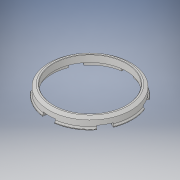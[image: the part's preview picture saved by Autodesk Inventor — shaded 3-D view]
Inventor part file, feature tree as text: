
AUTODESK INVENTOR PART (.ipt)
format: ipt  version: 2018 (Build 220112000, 112)  size: 431,616 bytes
history: native  units: mm
features: reference x28, sketch x14, projected_geometry x11, other x7, extrude x6, sweep x5, fillet x5, chamfer x3, pattern_circular x1
ambient origin geometry x8: Origin, YZ Plane, XZ Plane, XY Plane, X Axis, Y Axis, Z Axis, Center Point
bodies: Volumenkörper1 (feature_tree)
feature tree (80):
  extrude  "Extrusion1"  Depth=2.0mm TaperAngle=45.0deg
  chamfer  "Fase1"  Distance=2.0mm
  extrude  "Extrusion4"  TaperAngle=0.0deg  [1 undecoded]
  sweep  "Sweeping4"
  sketch  "Skizze16"  dims[d29=23.0mm]
  sketch  "Skizze17"  dims[d30=2.0mm d31=0.0mm d32=1.25mm d33=0.174533mm d34=0.174533mm d36=62.65732mm d37=0.174533mm d38=0.174533mm d39=2.0mm d40=0.0mm d43=2.0mm d44=0.0mm d45=0.5mm d46=0.4mm d47=0.5mm d48=0.5mm d49=60.0mm d50=360.0deg d52=0.5mm d53=0.5mm d54=0.0mm d55=0.0mm d56=0.2mm d57=0.0mm d58=0.0mm d59=1.0mm d60=0.25mm d61=2.0mm d62=0.0mm d63=1.25mm d64=1.75mm d65=45.0deg d66=1.0mm]
  sweep  "Sweeping5"
  fillet  "Rundung4"  Radius=0.5mm
  fillet  "Rundung5"  Radius=0.1mm
  extrude  "Extrusion6"  Depth=2.0mm TaperAngle=45.0deg
  pattern_circular  "Runde Anordnung1"  [2 undecoded]
  extrude  "Extrusion7"  Depth=1.25mm
  chamfer  "Fase3"  Distance=0.174533mm
  extrude  "Extrusion2"  Depth=1.25mm
  sketch  "Skizze3"  dims[d5=0.2mm]
  sketch  "Skizze4"  dims[d6=0.2mm]
  sketch  "Skizze6"  dims[d7=0.2mm d8=2.0mm d9=0.0mm]
  sweep  "Sweeping1"
  sweep  "Sweeping2"
  sweep  "Sweeping3"
  chamfer  "Fase2"  Distance=2.0mm
  fillet  "Rundung1"  Radius=0.5mm
  fillet  "Rundung2"  Radius=0.4mm
  extrude  "Extrusion3"  Depth=1.25mm
  fillet  "Rundung3"  Radius=0.5mm
  sketch  "Skizze10"  dims[d20=0.0mm d21=0.0mm d22=0.25mm d23=2.0mm d24=45.0deg]
  sketch  "Skizze1"  dims[d0=4.0mm d1=0.0mm d2=0.2mm d3=2.0mm d4=45.0deg]
  reference  "Referenz1"
  reference  "Referenz2"
  reference  "Referenz3"
  reference  "Referenz4"
  reference  "Referenz5"
  reference  "Referenz6"
  reference  "Referenz7"
  reference  "Referenz8"
  reference  "Referenz9"
  reference  "Referenz10"
  reference  "Referenz11"
  reference  "Referenz12"
  reference  "Referenz13"
  reference  "Referenz14"
  reference  "Referenz15"
  reference  "Referenz16"
  reference  "Referenz17"
  reference  "Referenz18"
  reference  "Referenz19"
  reference  "Referenz20"
  reference  "Referenz21"
  reference  "Referenz22"
  reference  "Referenz23"
  reference  "Referenz24"
  reference  "Referenz25"
  other  "3D-Skizze1"
  sketch  "Skizze7"  dims[d10=0.1mm d11=0.0mm d12=0.0mm]
  projected_geometry  "Projizierte Kontur1"
  reference  "Referenz26"
  other  "3D-Skizze2"
  sketch  "Skizze8"  dims[d13=0.1mm d14=0.5mm]
  projected_geometry  "Projizierte Kontur2"
  reference  "Referenz27"
  other  "3D-Skizze3"
  sketch  "Skizze9"  dims[d15=0.5mm d16=0.0mm d17=0.0mm d18=0.5mm d19=0.1mm]
  projected_geometry  "Projizierte Kontur3"
  projected_geometry  "Projizierte Kontur4"
  projected_geometry  "Projizierte Kontur5"
  projected_geometry  "Projizierte Kontur6"
  sketch  "Skizze12"  dims[d25=0.25mm]
  projected_geometry  "Projizierte Kontur7"
  sketch  "Skizze13"  dims[d26=0.25mm]
  reference  "Referenz29"
  sketch  "Skizze14"  dims[d27=23.0mm]
  sketch  "Skizze15"  dims[d28=23.0mm]
  projected_geometry  "Projizierte Kontur8"
  projected_geometry  "Projizierte Kontur9"
  projected_geometry  "Projizierte Kontur10"
  projected_geometry  "Projizierte Kontur11"
  other  "3D-Skizze4"
  parser-record x1  (decoder bookkeeping rows leaked as tree rows — omitted from the tree; the rows remain in map.json)
  other  "VolumeKnob.iam"
  other  "Oberbau:1"
note: 3 required parameter values undecoded (feature->parameter linkage not recoverable at this tier; creation-order binding heuristic only, values carry confidence <= 0.55)
note: 1 file-system path scrubbed to <path> (originals preserved in map.json)
